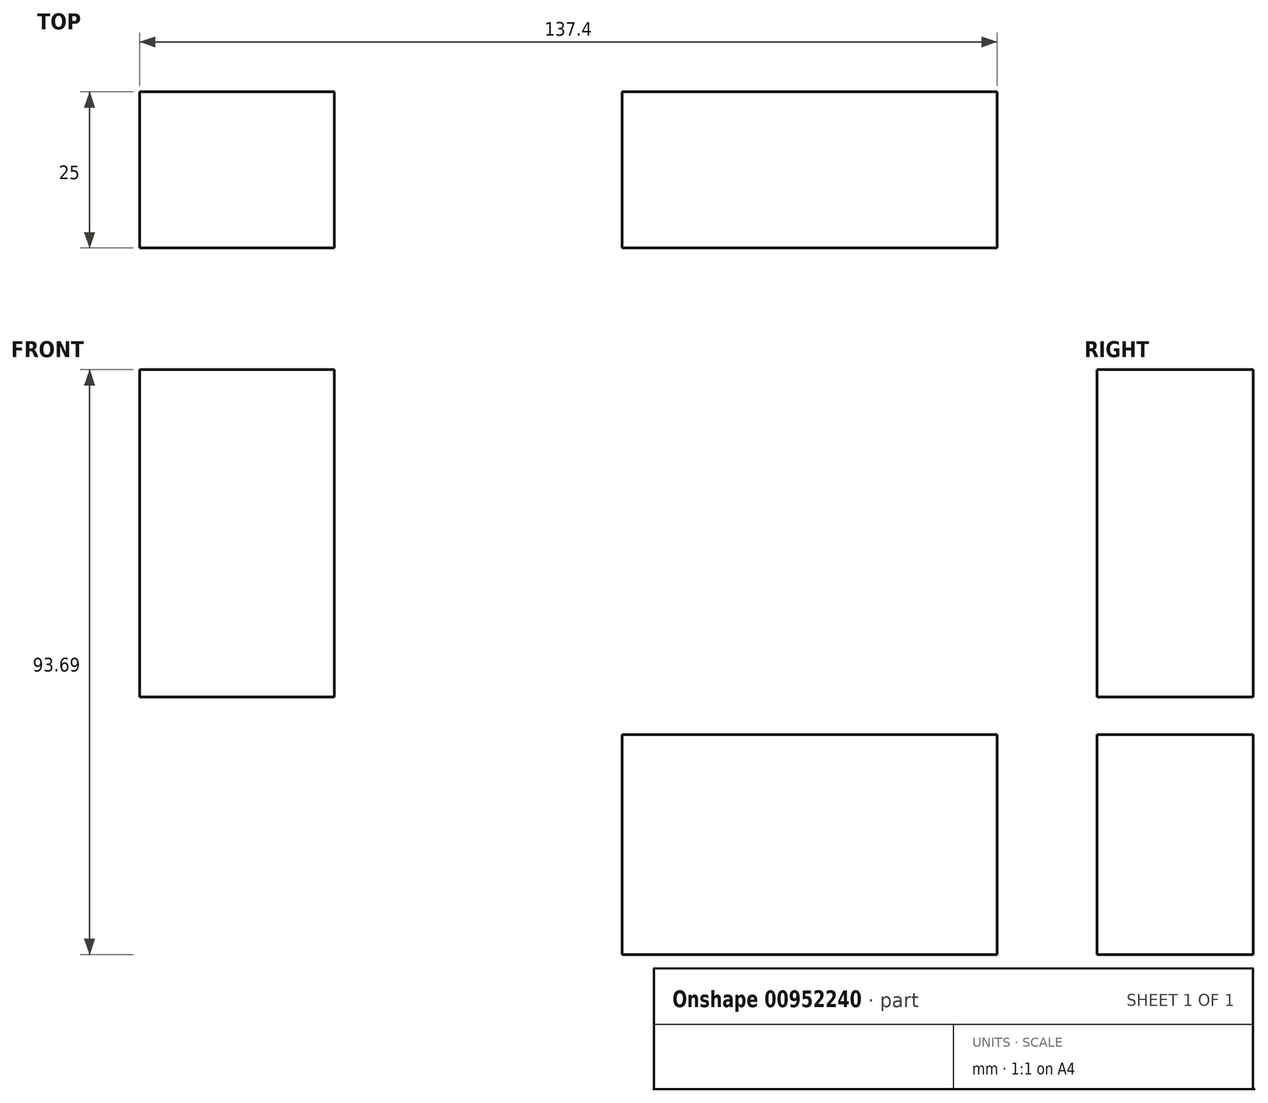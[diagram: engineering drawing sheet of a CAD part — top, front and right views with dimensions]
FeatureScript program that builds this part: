
annotation { "Feature Type Name" : "Feature", "Feature Type Description" : "" }
export const myFeature = defineFeature(function(context is Context, id is Id, definition is map)
    precondition{}
    {
        {
            var Q0;
            Q0=qCreatedBy(makeId("Front.planeOp"),FACE);
            var sketch = newSketch(context, id + "F0", { "sketchPlane" : qUnion([Q0])});
            skLineSegment(sketch, "E0.bottom", {"start": v(-73.02, 52.47) * mm, "end": v(-41.83, 52.47) * mm});
            skLineSegment(sketch, "E0.top", {"start": v(-73.02, 0) * mm, "end": v(-41.83, 0) * mm});
            skLineSegment(sketch, "E0.left", {"start": v(-73.02, 52.47) * mm, "end": v(-73.02, 0) * mm});
            skLineSegment(sketch, "E0.right", {"start": v(-41.83, 52.47) * mm, "end": v(-41.83, 0) * mm});
            skLineSegment(sketch, "E1.bottom", {"start": v(4.31, -6) * mm, "end": v(64.38, -6) * mm});
            skLineSegment(sketch, "E1.top", {"start": v(4.31, -41.22) * mm, "end": v(64.38, -41.22) * mm});
            skLineSegment(sketch, "E1.left", {"start": v(4.31, -6) * mm, "end": v(4.31, -41.22) * mm});
            skLineSegment(sketch, "E1.right", {"start": v(64.38, -6) * mm, "end": v(64.38, -41.22) * mm});
            skSolve(sketch);
        }
        {
            var Q0;
            Q0 = qSketchRegion(id + "F0", true);
            extrude(context, id + "F1", {"entities" : qUnion([Q0]), "depth" : 25 * mm, "offsetDistance" : 25 * mm});
        }
    });
